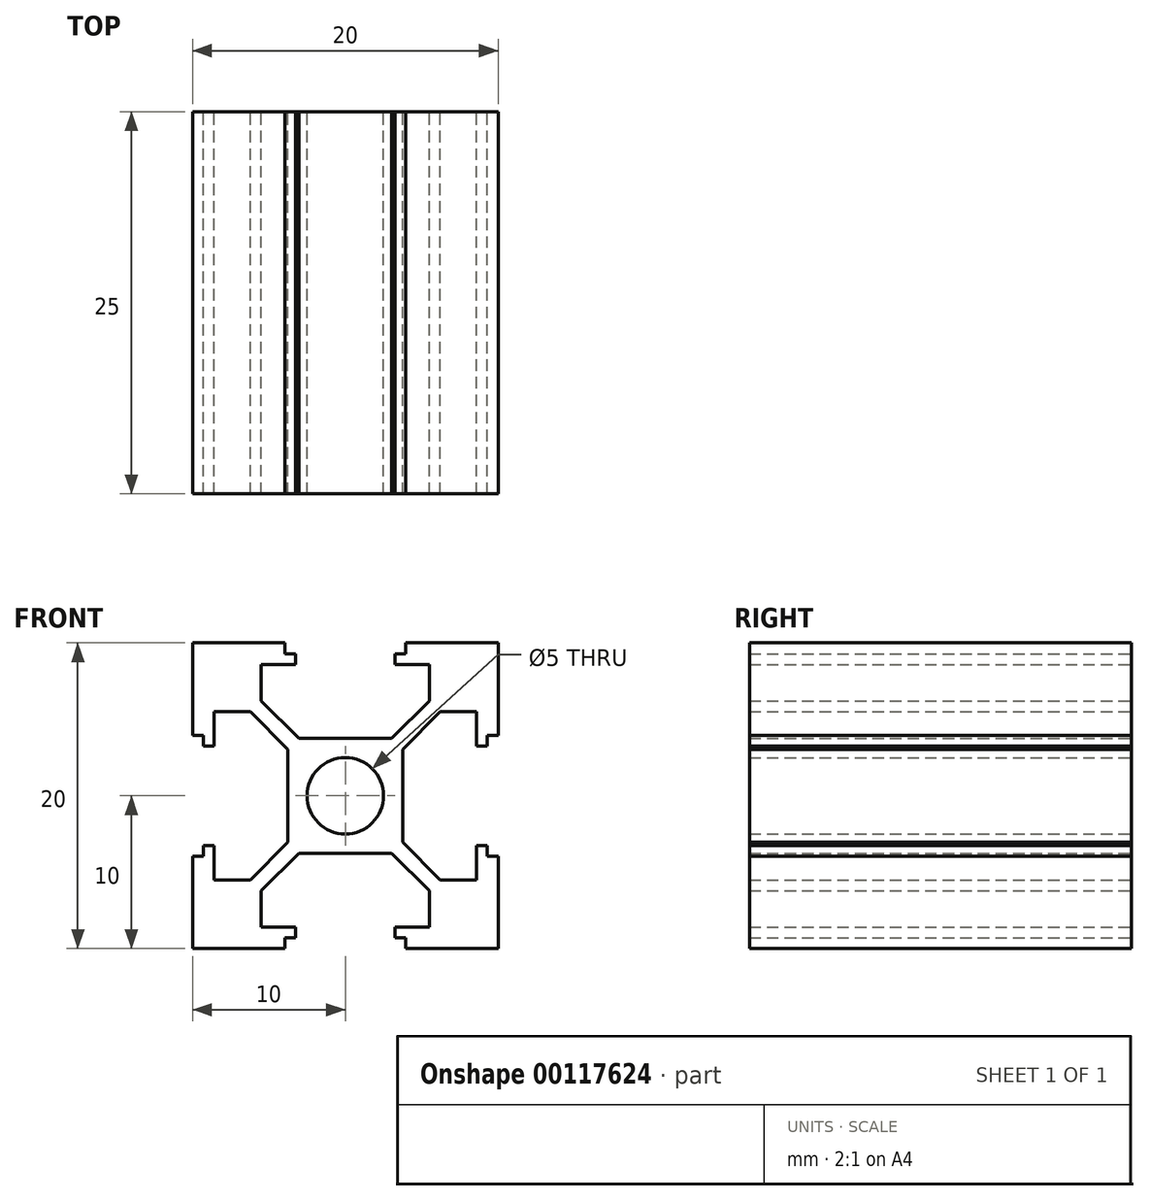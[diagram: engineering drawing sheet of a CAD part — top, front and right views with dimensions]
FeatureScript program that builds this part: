
annotation { "Feature Type Name" : "Feature", "Feature Type Description" : "" }
export const myFeature = defineFeature(function(context is Context, id is Id, definition is map)
    precondition{}
    {
        {
            var Q0;
            Q0=qCreatedBy(makeId("Front.planeOp"),FACE);
            var sketch = newSketch(context, id + "F0", { "sketchPlane" : qUnion([Q0])});
            skLineSegment(sketch, "E0.bottom", {"start": v(0, 10) * mm, "end": v(10, 10) * mm, "construction": true});
            skLineSegment(sketch, "E0.top", {"start": v(0, 0) * mm, "end": v(10, 0) * mm, "construction": true});
            skLineSegment(sketch, "E0.left", {"start": v(0, 10) * mm, "end": v(0, 0) * mm, "construction": true});
            skLineSegment(sketch, "E0.right", {"start": v(10, 10) * mm, "end": v(10, 0) * mm, "construction": true});
            skLineSegment(sketch, "E1", {"start": v(0, 0) * mm, "end": v(10, 10) * mm, "construction": true});
            skLineSegment(sketch, "E2", {"start": v(10, 10) * mm, "end": v(10, 3.95) * mm});
            skLineSegment(sketch, "E3", {"start": v(10, 3.95) * mm, "end": v(9.3, 3.95) * mm});
            skLineSegment(sketch, "E4", {"start": v(9.3, 3.95) * mm, "end": v(9.3, 3.25) * mm});
            skLineSegment(sketch, "E5", {"start": v(9.3, 3.25) * mm, "end": v(8.6, 3.25) * mm});
            skLineSegment(sketch, "E6", {"start": v(8.6, 3.25) * mm, "end": v(8.6, 5.5) * mm});
            skLineSegment(sketch, "E7", {"start": v(8.6, 5.5) * mm, "end": v(6.2, 5.5) * mm});
            skLineSegment(sketch, "E8", {"start": v(6.2, 5.5) * mm, "end": v(3.75, 3.04) * mm});
            skLineSegment(sketch, "E9", {"start": v(3.75, 3.04) * mm, "end": v(3.75, 0) * mm});
            skLineSegment(sketch, "E10.MirrorCS", {"start": v(10, 10) * mm, "end": v(3.95, 10) * mm});
            skLineSegment(sketch, "E11.MirrorCS", {"start": v(3.04, 3.75) * mm, "end": v(0, 3.75) * mm});
            skLineSegment(sketch, "E12.MirrorCS", {"start": v(5.5, 6.2) * mm, "end": v(3.04, 3.75) * mm});
            skLineSegment(sketch, "E13.MirrorCS", {"start": v(5.5, 8.6) * mm, "end": v(5.5, 6.2) * mm});
            skLineSegment(sketch, "E14.MirrorCS", {"start": v(3.25, 8.6) * mm, "end": v(5.5, 8.6) * mm});
            skLineSegment(sketch, "E15.MirrorCS", {"start": v(3.25, 9.3) * mm, "end": v(3.25, 8.6) * mm});
            skLineSegment(sketch, "E16.MirrorCS", {"start": v(3.95, 10) * mm, "end": v(3.95, 9.3) * mm});
            skLineSegment(sketch, "E17.MirrorCS", {"start": v(3.95, 9.3) * mm, "end": v(3.25, 9.3) * mm});
            skLineSegment(sketch, "E18.1.0", {"start": v(-6.2, 5.5) * mm, "end": v(-3.75, 3.04) * mm});
            skLineSegment(sketch, "E18.1.1", {"start": v(-3.25, 9.3) * mm, "end": v(-3.25, 8.6) * mm});
            skLineSegment(sketch, "E18.1.2", {"start": v(-3.75, 3.04) * mm, "end": v(-3.75, 0) * mm});
            skLineSegment(sketch, "E18.1.3", {"start": v(-5.5, 8.6) * mm, "end": v(-5.5, 6.2) * mm});
            skLineSegment(sketch, "E18.1.4", {"start": v(-5.5, 6.2) * mm, "end": v(-3.04, 3.75) * mm});
            skLineSegment(sketch, "E18.1.5", {"start": v(-3.04, 3.75) * mm, "end": v(0, 3.75) * mm});
            skLineSegment(sketch, "E18.1.6", {"start": v(-3.25, 8.6) * mm, "end": v(-5.5, 8.6) * mm});
            skLineSegment(sketch, "E18.1.7", {"start": v(-3.95, 10) * mm, "end": v(-3.95, 9.3) * mm});
            skLineSegment(sketch, "E18.1.8", {"start": v(-3.95, 9.3) * mm, "end": v(-3.25, 9.3) * mm});
            skLineSegment(sketch, "E18.1.9", {"start": v(-10, 0) * mm, "end": v(-10, 10) * mm, "construction": true});
            skLineSegment(sketch, "E18.1.10", {"start": v(-8.6, 3.25) * mm, "end": v(-8.6, 5.5) * mm});
            skLineSegment(sketch, "E18.1.11", {"start": v(-8.6, 5.5) * mm, "end": v(-6.2, 5.5) * mm});
            skLineSegment(sketch, "E18.1.12", {"start": v(-10, 0) * mm, "end": v(0, 0) * mm, "construction": true});
            skLineSegment(sketch, "E18.1.13", {"start": v(-9.3, 3.25) * mm, "end": v(-8.6, 3.25) * mm});
            skLineSegment(sketch, "E18.1.14", {"start": v(-10, 10) * mm, "end": v(0, 10) * mm, "construction": true});
            skLineSegment(sketch, "E18.1.15", {"start": v(0, 0) * mm, "end": v(-10, 10) * mm, "construction": true});
            skLineSegment(sketch, "E18.1.16", {"start": v(-10, 10) * mm, "end": v(-10, 3.95) * mm});
            skLineSegment(sketch, "E18.1.17", {"start": v(-10, 10) * mm, "end": v(-3.95, 10) * mm});
            skLineSegment(sketch, "E18.1.18", {"start": v(-10, 3.95) * mm, "end": v(-9.3, 3.95) * mm});
            skLineSegment(sketch, "E18.1.19", {"start": v(-9.3, 3.95) * mm, "end": v(-9.3, 3.25) * mm});
            skLineSegment(sketch, "E18.1.20", {"start": v(0, 0) * mm, "end": v(0, 10) * mm, "construction": true});
            skLineSegment(sketch, "E18.2.0", {"start": v(-5.5, -6.2) * mm, "end": v(-3.04, -3.75) * mm});
            skLineSegment(sketch, "E18.2.1", {"start": v(-9.3, -3.25) * mm, "end": v(-8.6, -3.25) * mm});
            skLineSegment(sketch, "E18.2.2", {"start": v(-3.04, -3.75) * mm, "end": v(0, -3.75) * mm});
            skLineSegment(sketch, "E18.2.3", {"start": v(-8.6, -5.5) * mm, "end": v(-6.2, -5.5) * mm});
            skLineSegment(sketch, "E18.2.4", {"start": v(-6.2, -5.5) * mm, "end": v(-3.75, -3.04) * mm});
            skLineSegment(sketch, "E18.2.5", {"start": v(-3.75, -3.04) * mm, "end": v(-3.75, 0) * mm});
            skLineSegment(sketch, "E18.2.6", {"start": v(-8.6, -3.25) * mm, "end": v(-8.6, -5.5) * mm});
            skLineSegment(sketch, "E18.2.7", {"start": v(-10, -3.95) * mm, "end": v(-9.3, -3.95) * mm});
            skLineSegment(sketch, "E18.2.8", {"start": v(-9.3, -3.95) * mm, "end": v(-9.3, -3.25) * mm});
            skLineSegment(sketch, "E18.2.9", {"start": v(0, -10) * mm, "end": v(-10, -10) * mm, "construction": true});
            skLineSegment(sketch, "E18.2.10", {"start": v(-3.25, -8.6) * mm, "end": v(-5.5, -8.6) * mm});
            skLineSegment(sketch, "E18.2.11", {"start": v(-5.5, -8.6) * mm, "end": v(-5.5, -6.2) * mm});
            skLineSegment(sketch, "E18.2.12", {"start": v(0, -10) * mm, "end": v(0, 0) * mm, "construction": true});
            skLineSegment(sketch, "E18.2.13", {"start": v(-3.25, -9.3) * mm, "end": v(-3.25, -8.6) * mm});
            skLineSegment(sketch, "E18.2.14", {"start": v(-10, -10) * mm, "end": v(-10, 0) * mm, "construction": true});
            skLineSegment(sketch, "E18.2.15", {"start": v(0, 0) * mm, "end": v(-10, -10) * mm, "construction": true});
            skLineSegment(sketch, "E18.2.16", {"start": v(-10, -10) * mm, "end": v(-3.95, -10) * mm});
            skLineSegment(sketch, "E18.2.17", {"start": v(-10, -10) * mm, "end": v(-10, -3.95) * mm});
            skLineSegment(sketch, "E18.2.18", {"start": v(-3.95, -10) * mm, "end": v(-3.95, -9.3) * mm});
            skLineSegment(sketch, "E18.2.19", {"start": v(-3.95, -9.3) * mm, "end": v(-3.25, -9.3) * mm});
            skLineSegment(sketch, "E18.2.20", {"start": v(0, 0) * mm, "end": v(-10, 0) * mm, "construction": true});
            skLineSegment(sketch, "E18.3.0", {"start": v(6.2, -5.5) * mm, "end": v(3.75, -3.04) * mm});
            skLineSegment(sketch, "E18.3.1", {"start": v(3.25, -9.3) * mm, "end": v(3.25, -8.6) * mm});
            skLineSegment(sketch, "E18.3.2", {"start": v(3.75, -3.04) * mm, "end": v(3.75, 0) * mm});
            skLineSegment(sketch, "E18.3.3", {"start": v(5.5, -8.6) * mm, "end": v(5.5, -6.2) * mm});
            skLineSegment(sketch, "E18.3.4", {"start": v(5.5, -6.2) * mm, "end": v(3.04, -3.75) * mm});
            skLineSegment(sketch, "E18.3.5", {"start": v(3.04, -3.75) * mm, "end": v(0, -3.75) * mm});
            skLineSegment(sketch, "E18.3.6", {"start": v(3.25, -8.6) * mm, "end": v(5.5, -8.6) * mm});
            skLineSegment(sketch, "E18.3.7", {"start": v(3.95, -10) * mm, "end": v(3.95, -9.3) * mm});
            skLineSegment(sketch, "E18.3.8", {"start": v(3.95, -9.3) * mm, "end": v(3.25, -9.3) * mm});
            skLineSegment(sketch, "E18.3.9", {"start": v(10, 0) * mm, "end": v(10, -10) * mm, "construction": true});
            skLineSegment(sketch, "E18.3.10", {"start": v(8.6, -3.25) * mm, "end": v(8.6, -5.5) * mm});
            skLineSegment(sketch, "E18.3.11", {"start": v(8.6, -5.5) * mm, "end": v(6.2, -5.5) * mm});
            skLineSegment(sketch, "E18.3.12", {"start": v(10, 0) * mm, "end": v(0, 0) * mm, "construction": true});
            skLineSegment(sketch, "E18.3.13", {"start": v(9.3, -3.25) * mm, "end": v(8.6, -3.25) * mm});
            skLineSegment(sketch, "E18.3.14", {"start": v(10, -10) * mm, "end": v(0, -10) * mm, "construction": true});
            skLineSegment(sketch, "E18.3.15", {"start": v(0, 0) * mm, "end": v(10, -10) * mm, "construction": true});
            skLineSegment(sketch, "E18.3.16", {"start": v(10, -10) * mm, "end": v(10, -3.95) * mm});
            skLineSegment(sketch, "E18.3.17", {"start": v(10, -10) * mm, "end": v(3.95, -10) * mm});
            skLineSegment(sketch, "E18.3.18", {"start": v(10, -3.95) * mm, "end": v(9.3, -3.95) * mm});
            skLineSegment(sketch, "E18.3.19", {"start": v(9.3, -3.95) * mm, "end": v(9.3, -3.25) * mm});
            skLineSegment(sketch, "E18.3.20", {"start": v(0, 0) * mm, "end": v(0, -10) * mm, "construction": true});
            skPoint(sketch, "E18.center", {"position": v(0, 0) * mm});
            skCircle(sketch, "E19", {"center": v(0, 0) * mm, "radius": 2.5 * mm});
            skSolve(sketch);
        }
        {
            var Q0;
            Q0=makeQuery(id+"F0.imprint","IMPRINT",FACE,{"disambiguationData":[TD([[makeQuery(id+"F0.imprint","IMPRINT",EDGE,{"derivedFrom":sQuery(id+"F0.wireOp",EDGE,"E2")}),-1.0]])]});
            extrude(context, id + "F1", {"entities" : qUnion([Q0]), "depth" : 25 * mm});
        }
    });
